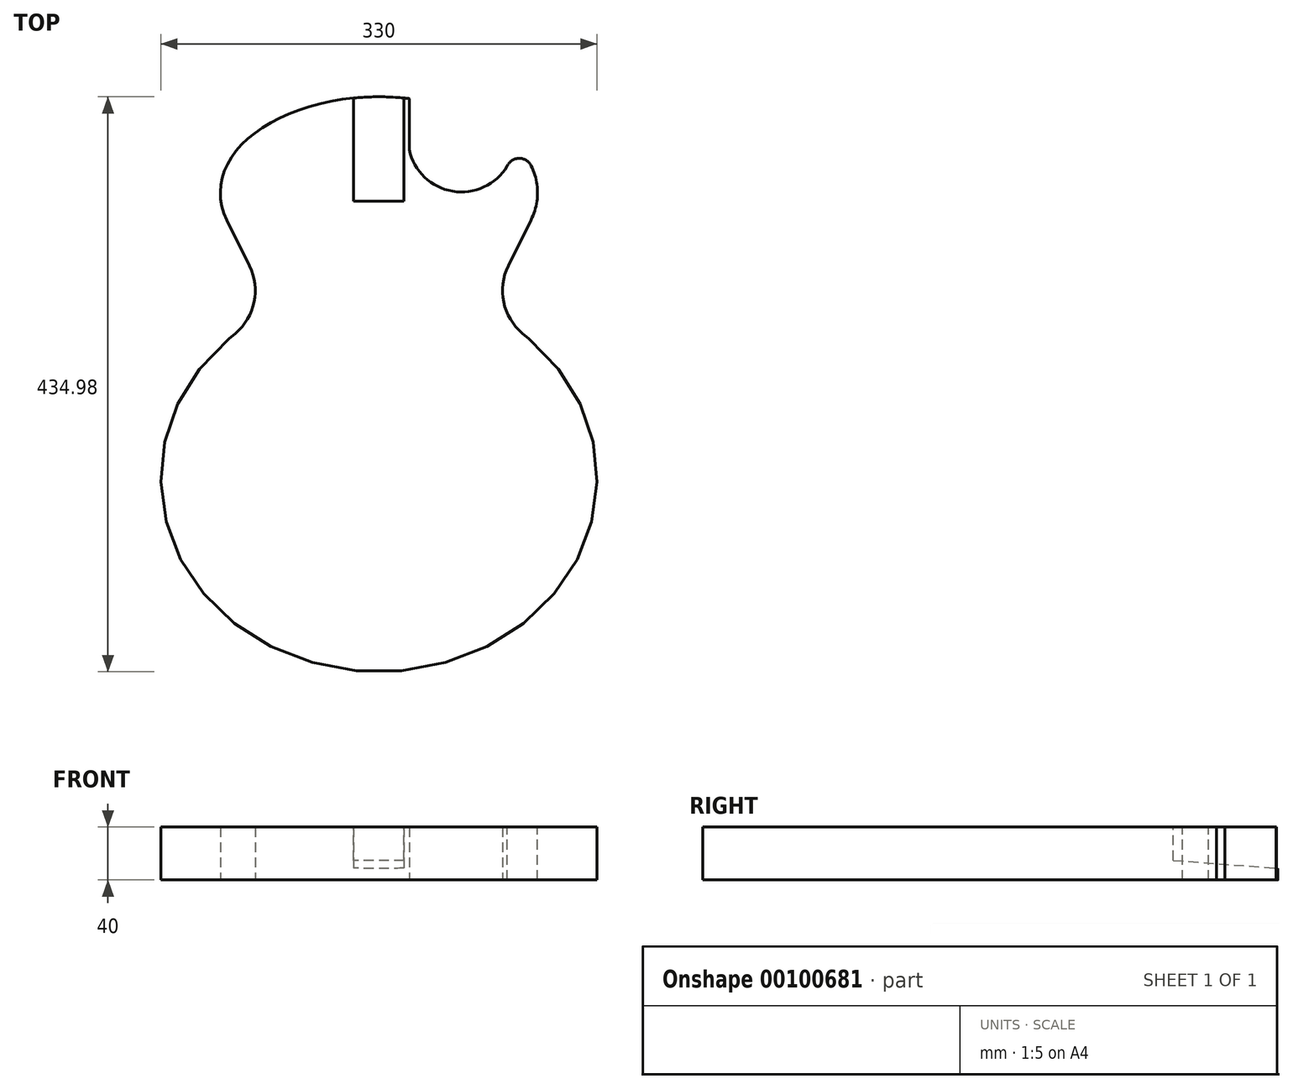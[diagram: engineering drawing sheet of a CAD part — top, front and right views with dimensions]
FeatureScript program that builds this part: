
annotation { "Feature Type Name" : "Feature", "Feature Type Description" : "" }
export const myFeature = defineFeature(function(context is Context, id is Id, definition is map)
    precondition{}
    {
        {
            var Q0;
            Q0=qCreatedBy(makeId("Top.planeOp"),FACE);
            var sketch = newSketch(context, id + "F0", { "sketchPlane" : qUnion([Q0])});
            skEllipticalArc(sketch, "E0", {});
            skEllipticalArc(sketch, "E1", {});
            skLineSegment(sketch, "E2", {"start": v(0, 0) * mm, "end": v(0, 434.98) * mm, "construction": true});
            skLineSegment(sketch, "E3", {"start": v(-244.22, 0) * mm, "end": v(-244.22, 277.4) * mm, "construction": true});
            skLineSegment(sketch, "E4", {"start": v(-244.22, 277.4) * mm, "end": v(0, 277.4) * mm, "construction": true});
            skLineSegment(sketch, "E5", {"start": v(-83.2, 277.4) * mm, "end": v(-113.54, 251.94) * mm, "construction": true});
            skLineSegment(sketch, "E6", {"start": v(-97.86, 307.08) * mm, "end": v(-114.99, 341.74) * mm});
            skArc(sketch, "E7", {"start": v(-108.56, 256.12) * mm, "mid": v(-94.4, 279.75) * mm, "end": v(-97.86, 307.08) * mm});
            skEllipticalArc(sketch, "E8.MirrorCS", {});
            skLineSegment(sketch, "E9.MirrorCS", {"start": v(97.86, 307.08) * mm, "end": v(114.99, 341.74) * mm});
            skArc(sketch, "E10.MirrorCS", {"start": v(108.56, 256.12) * mm, "mid": v(94.4, 279.75) * mm, "end": v(97.86, 307.08) * mm});
            skEllipticalArc(sketch, "E11.MirrorCS", {});
            skPoint(sketch, "E12.orphan", {"position": v(120.66, 353.23) * mm});
            skPoint(sketch, "E13.orphan", {"position": v(-120.66, 353.23) * mm});
            skLineSegment(sketch, "E14", {"start": v(-113.54, 251.94) * mm, "end": v(-108.56, 256.12) * mm});
            skLineSegment(sketch, "E15", {"start": v(108.56, 256.12) * mm, "end": v(113.54, 251.94) * mm});
            const initialGuessF0  = {"E0": [0, 0.146, 0, -1, 0.146, 0.165, 3.900459787077389, 6.283185307179586], "E1": [0, 0.362475, -1, 0, 0.12, 0.0725, 4.71238898038469, 0.290121487978938], "E8.MirrorCS": [0, 0.362475, 1, 0, 0.12, 0.0725, 5.993063819200649, 1.5707963267948966], "E11.MirrorCS": [0, 0.146, 0, -1, 0.146, 0.165, 6.283185307179586, 2.3827255201021975]};
            skSetInitialGuess(sketch, initialGuessF0);
            skSolve(sketch);
        }
        {
            var Q0;
            Q0=qSketchRegion(id+"F0",true);
            extrude(context, id + "F1", {"entities" : qUnion([Q0]), "depth" : 40 * mm});
        }
        {
            var Q0;
            Q0=makeQuery(id+"F1.opExtrude","CAP_FACE",FACE,{"disambiguationData":[OSD([sQuery(id+"F0.wireOp",EDGE,"E0"),sQuery(id+"F0.wireOp",EDGE,"E1"),sQuery(id+"F0.wireOp",EDGE,"E6"),sQuery(id+"F0.wireOp",EDGE,"E7"),sQuery(id+"F0.wireOp",EDGE,"E8.MirrorCS"),sQuery(id+"F0.wireOp",EDGE,"E9.MirrorCS"),sQuery(id+"F0.wireOp",EDGE,"E10.MirrorCS"),sQuery(id+"F0.wireOp",EDGE,"E11.MirrorCS"),sQuery(id+"F0.wireOp",EDGE,"E14"),sQuery(id+"F0.wireOp",EDGE,"E15")])],"isStart":false});
            var sketch = newSketch(context, id + "F2", { "sketchPlane" : qUnion([Q0])});
            skLineSegment(sketch, "E16", {"start": v(0, 434.98) * mm, "end": v(0, 369.98) * mm, "construction": true});
            skPoint(sketch, "E16.endSnap0", {"position": v(0, 434.98) * mm});
            skLineSegment(sketch, "E17.0", {"start": v(23, 434.98) * mm, "end": v(23, 394.98) * mm});
            skLineSegment(sketch, "E18", {"start": v(0, 434.98) * mm, "end": v(23, 434.98) * mm, "construction": true});
            skArc(sketch, "E19", {"start": v(115.17, 382.83) * mm, "mid": v(106.01, 388.47) * mm, "end": v(97.04, 382.55) * mm});
            skLineSegment(sketch, "E20", {"start": v(115.17, 382.83) * mm, "end": v(89.92, 434.98) * mm});
            skLineSegment(sketch, "E21", {"start": v(23, 434.98) * mm, "end": v(89.92, 434.98) * mm});
            skLineSegment(sketch, "E22", {"start": v(23, 394.98) * mm, "end": v(23, 362.97) * mm, "construction": true});
            skPoint(sketch, "E23.end.orphan", {"position": v(120, 362.48) * mm});
            skPoint(sketch, "E24.center.orphan", {"position": v(45.5, 394.98) * mm});
            skLineSegment(sketch, "E25", {"start": v(23, 362.98) * mm, "end": v(120, 362.98) * mm, "construction": true});
            skLineSegment(sketch, "E26", {"start": v(120, 362.98) * mm, "end": v(120, 362.98) * mm});
            skArc(sketch, "E27", {"start": v(23, 394.98) * mm, "mid": v(55.78, 363.53) * mm, "end": v(97.04, 382.55) * mm});
            skSolve(sketch);
        }
        {
            var Q0;
            Q0=qSketchRegion(id+"F2",true);
            extrude(context, id + "F3", {"entities" : qUnion([Q0]), "operationType" : NewBodyOperationType.REMOVE, "endBound" : BoundingType.THROUGH_ALL, "oppositeDirection" : true, "depth" : 25 * mm});
        }
        {
            var Q0;
            Q0=makeQuery(id+"F1.opExtrude","CAP_FACE",FACE,{"disambiguationData":[OSD([sQuery(id+"F0.wireOp",EDGE,"E0"),sQuery(id+"F0.wireOp",EDGE,"E1"),sQuery(id+"F0.wireOp",EDGE,"E6"),sQuery(id+"F0.wireOp",EDGE,"E7"),sQuery(id+"F0.wireOp",EDGE,"E8.MirrorCS"),sQuery(id+"F0.wireOp",EDGE,"E9.MirrorCS"),sQuery(id+"F0.wireOp",EDGE,"E10.MirrorCS"),sQuery(id+"F0.wireOp",EDGE,"E11.MirrorCS"),sQuery(id+"F0.wireOp",EDGE,"E14"),sQuery(id+"F0.wireOp",EDGE,"E15")])],"isStart":false});
            var sketch = newSketch(context, id + "F4", { "sketchPlane" : qUnion([Q0])});
            skLineSegment(sketch, "E28", {"start": v(0, 0) * mm, "end": v(0, 434.98) * mm, "construction": true});
            skLineSegment(sketch, "E29.bottom", {"start": v(19.05, 513.98) * mm, "end": v(-19.05, 513.98) * mm});
            skLineSegment(sketch, "E29.top", {"start": v(19.05, 355.98) * mm, "end": v(-19.05, 355.98) * mm});
            skLineSegment(sketch, "E29.left", {"start": v(19.05, 513.98) * mm, "end": v(19.05, 355.98) * mm});
            skLineSegment(sketch, "E29.right", {"start": v(-19.05, 513.98) * mm, "end": v(-19.05, 355.98) * mm});
            skPoint(sketch, "E29.middle", {"position": v(0, 434.98) * mm});
            skSolve(sketch);
        }
        {
            var Q0;
            Q0 = qSketchRegion(id + "F4", true);
            extrude(context, id + "F6", {"entities" : qUnion([Q0]), "operationType" : NewBodyOperationType.REMOVE, "oppositeDirection" : true, "depth" : 25.12 * mm});
        }
        {
            var Q0;
            Q0=makeQuery(id+"F6.boolean.opBoolean","COPY",FACE,{"derivedFrom":makeQuery(id+"F6.opExtrude","CAP_FACE",FACE,{"disambiguationData":[OSD([sQuery(id+"F4.wireOp",EDGE,"E29.bottom"),sQuery(id+"F4.wireOp",EDGE,"E29.top"),sQuery(id+"F4.wireOp",EDGE,"E29.left"),sQuery(id+"F4.wireOp",EDGE,"E29.right")])],"isStart":false})});
            var sketch = newSketch(context, id + "F7", { "sketchPlane" : qUnion([Q0])});
            skPoint(sketch, "E30", {"position": v(-19.05, 355.98) * mm});
            skSolve(sketch);
        }
        {
            var Q0;
            Q0=makeQuery(id+"F6.boolean.opBoolean","COPY",FACE,{"derivedFrom":makeQuery(id+"F6.opExtrude","SWEPT_FACE",FACE,{"disambiguationData":[OSD([sQuery(id+"F4.wireOp",EDGE,"E29.right")])]})});
            var sketch = newSketch(context, id + "F8", { "sketchPlane" : qUnion([Q0])});
            skLineSegment(sketch, "E31", {"start": v(355.98, 14.88) * mm, "end": v(455.68, 7.2) * mm});
            skLineSegment(sketch, "E32", {"start": v(355.98, 14.88) * mm, "end": v(455.68, 14.88) * mm});
            skLineSegment(sketch, "E33", {"start": v(455.68, 7.2) * mm, "end": v(455.68, 14.88) * mm});
            skSolve(sketch);
        }
        {
            var Q0;
            Q0 = qSketchRegion(id + "F8", true);
            extrude(context, id + "F5", {"entities" : qUnion([Q0]), "operationType" : NewBodyOperationType.REMOVE, "depth" : 38.1 * mm});
        }
    });
